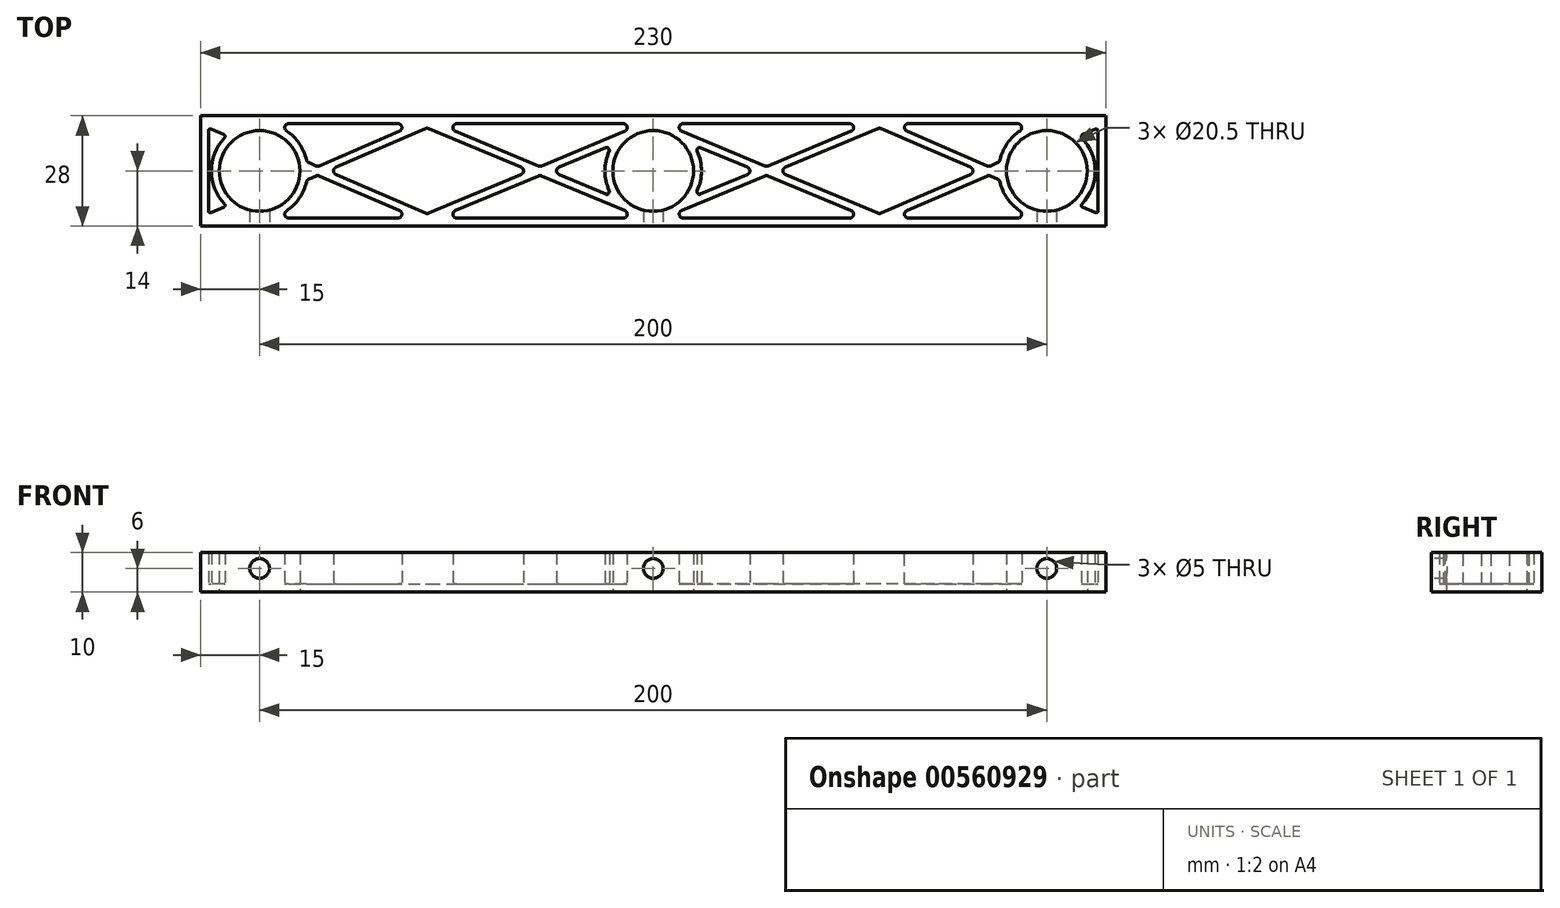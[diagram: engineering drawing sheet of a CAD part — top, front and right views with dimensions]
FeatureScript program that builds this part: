
annotation { "Feature Type Name" : "Feature", "Feature Type Description" : "" }
export const myFeature = defineFeature(function(context is Context, id is Id, definition is map)
    precondition{}
    {
        {
            var Q0;
            Q0=qCreatedBy(makeId("Top.planeOp"),FACE);
            var sketch = newSketch(context, id + "F0", { "sketchPlane" : qUnion([Q0])});
            skCircle(sketch, "E0", {"center": v(0, 0) * mm, "radius": 10.25 * mm});
            skCircle(sketch, "E1", {"center": v(-100, 0) * mm, "radius": 10.25 * mm});
            skLineSegment(sketch, "E2", {"start": v(0, 0) * mm, "end": v(0, 43.05) * mm, "construction": true});
            skCircle(sketch, "E3.MirrorC", {"center": v(100, 0) * mm, "radius": 10.25 * mm});
            skLineSegment(sketch, "E4", {"start": v(-100, 0) * mm, "end": v(0, 0) * mm, "construction": true});
            skLineSegment(sketch, "E5.bottom", {"start": v(115, -14) * mm, "end": v(-115, -14) * mm});
            skLineSegment(sketch, "E5.top", {"start": v(115, 14) * mm, "end": v(-115, 14) * mm});
            skLineSegment(sketch, "E5.left", {"start": v(115, -14) * mm, "end": v(115, 14) * mm});
            skLineSegment(sketch, "E5.right", {"start": v(-115, -14) * mm, "end": v(-115, 14) * mm});
            skSolve(sketch);
        }
        {
            var Q0;
            Q0=makeQuery(id+"F0.imprint","IMPRINT",FACE,{"disambiguationData":[TD([[makeQuery(id+"F0.imprint","IMPRINT",EDGE,{"derivedFrom":sQuery(id+"F0.wireOp",EDGE,"E0")}),-1.0]])]});
            extrude(context, id + "F1", {"entities" : qUnion([Q0]), "depth" : 2 * mm});
        }
        {
            var Q0;
            Q0=makeQuery(id+"F1.opExtrude","CAP_FACE",FACE,{"disambiguationData":[OSD([sQuery(id+"F0.wireOp",EDGE,"E0"),sQuery(id+"F0.wireOp",EDGE,"E1"),sQuery(id+"F0.wireOp",EDGE,"E3.MirrorC"),sQuery(id+"F0.wireOp",EDGE,"E5.bottom"),sQuery(id+"F0.wireOp",EDGE,"E5.top"),sQuery(id+"F0.wireOp",EDGE,"E5.left"),sQuery(id+"F0.wireOp",EDGE,"E5.right")])],"isStart":false});
            var sketch = newSketch(context, id + "F2", { "sketchPlane" : qUnion([Q0])});
            skLineSegment(sketch, "E6.0", {"start": v(115, 14) * mm, "end": v(-115, 14) * mm});
            skLineSegment(sketch, "E7.0", {"start": v(-115, -14) * mm, "end": v(-115, 14) * mm});
            skLineSegment(sketch, "E8.0", {"start": v(115, -14) * mm, "end": v(-115, -14) * mm});
            skLineSegment(sketch, "E9.0", {"start": v(115, -14) * mm, "end": v(115, 14) * mm});
            skLineSegment(sketch, "E10.bottom", {"start": v(-110.48, 12) * mm, "end": v(-102.46, 12) * mm, "construction": true});
            skLineSegment(sketch, "E10.top", {"start": v(-110.48, -12) * mm, "end": v(-102.46, -12) * mm, "construction": true});
            skLineSegment(sketch, "E10.left", {"start": v(-113, 10.91) * mm, "end": v(-113, -10.91) * mm});
            skLineSegment(sketch, "E10.right", {"start": v(113, 10.91) * mm, "end": v(113, -10.91) * mm});
            skPoint(sketch, "E10.middle", {"position": v(0, 0) * mm});
            skCircle(sketch, "E11.0", {"center": v(-100, 0) * mm, "radius": 10.25 * mm});
            skCircle(sketch, "E12.0", {"center": v(0, 0) * mm, "radius": 10.25 * mm});
            skCircle(sketch, "E13.0", {"center": v(100, 0) * mm, "radius": 10.25 * mm});
            skArc(sketch, "E14", {"start": v(-87.96, 2.26) * mm, "mid": v(-91.27, 8.59) * mm, "end": v(-97.54, 12) * mm});
            skArc(sketch, "E15", {"start": v(-11.1, 5.2) * mm, "mid": v(-12.25, 0) * mm, "end": v(-11.1, -5.2) * mm});
            skArc(sketch, "E16", {"start": v(106.6, 10.32) * mm, "mid": v(104.6, 11.35) * mm, "end": v(102.46, 12) * mm, "construction": true});
            skLineSegment(sketch, "E17", {"start": v(0, 29.32) * mm, "end": v(0, -26.43) * mm, "construction": true});
            skLineSegment(sketch, "E18", {"start": v(-57.5, -14) * mm, "end": v(-57.5, 14) * mm, "construction": true});
            skLineSegment(sketch, "E19.MirrorCS", {"start": v(57.5, -14) * mm, "end": v(57.5, 14) * mm, "construction": true});
            skLineSegment(sketch, "E20", {"start": v(-113, 12) * mm, "end": v(-57.5, -12) * mm, "construction": true});
            skLineSegment(sketch, "E21", {"start": v(-57.5, 12) * mm, "end": v(-113, -12) * mm, "construction": true});
            skLineSegment(sketch, "E22", {"start": v(-57.5, 12) * mm, "end": v(0, -12) * mm, "construction": true});
            skLineSegment(sketch, "E23", {"start": v(-57.5, -12) * mm, "end": v(0, 12) * mm, "construction": true});
            skLineSegment(sketch, "E24", {"start": v(-110.48, -12) * mm, "end": v(-106.6, -10.32) * mm, "construction": true});
            skLineSegment(sketch, "E25.MirrorCS", {"start": v(-111.27, -10.16) * mm, "end": v(-108.4, -8.92) * mm});
            skPoint(sketch, "E26.orphan", {"position": v(-58.3, 12.75) * mm});
            skLineSegment(sketch, "E27", {"start": v(-111.27, -10.16) * mm, "end": v(-113, -10.91) * mm});
            skLineSegment(sketch, "E28", {"start": v(-110.48, 12) * mm, "end": v(-106.6, 10.32) * mm, "construction": true});
            skLineSegment(sketch, "E29.MirrorCS", {"start": v(-111.27, 10.16) * mm, "end": v(-108.4, 8.92) * mm});
            skLineSegment(sketch, "E30", {"start": v(-111.27, 10.16) * mm, "end": v(-113, 10.91) * mm});
            skPoint(sketch, "E31.orphan", {"position": v(-58.3, -12.75) * mm});
            skLineSegment(sketch, "E32.trimOffspring", {"start": v(-85.25, 1.09) * mm, "end": v(-60.02, 12) * mm});
            skLineSegment(sketch, "E33.trimOffspring", {"start": v(-82.73, 0) * mm, "end": v(-57.5, -10.91) * mm});
            skLineSegment(sketch, "E34.trimOffspring", {"start": v(-82.73, 0) * mm, "end": v(-57.5, 10.91) * mm});
            skLineSegment(sketch, "E35.trimOffspring", {"start": v(-85.25, -1.09) * mm, "end": v(-60.02, -12) * mm});
            skLineSegment(sketch, "E36.trimOffspring", {"start": v(-87.96, 2.26) * mm, "end": v(-85.25, 1.09) * mm});
            skLineSegment(sketch, "E37.trimOffspring", {"start": v(-87.96, -2.26) * mm, "end": v(-85.25, -1.09) * mm});
            skArc(sketch, "E38.trimOffspring", {"start": v(-108.4, 8.92) * mm, "mid": v(-112.25, 0) * mm, "end": v(-108.4, -8.92) * mm});
            skArc(sketch, "E39.trimOffspring", {"start": v(-106.6, -10.32) * mm, "mid": v(-104.6, -11.35) * mm, "end": v(-102.46, -12) * mm, "construction": true});
            skLineSegment(sketch, "E40", {"start": v(-57.5, 10.91) * mm, "end": v(-31.36, 0) * mm});
            skLineSegment(sketch, "E41.MirrorCS", {"start": v(-54.89, 12) * mm, "end": v(-28.75, 1.09) * mm});
            skPoint(sketch, "E42.orphan", {"position": v(-56.73, 12.77) * mm});
            skLineSegment(sketch, "E43.trimOffspring", {"start": v(-54.89, 12) * mm, "end": v(-2.61, 12) * mm});
            skLineSegment(sketch, "E44", {"start": v(-57.5, -10.91) * mm, "end": v(-31.36, 0) * mm});
            skLineSegment(sketch, "E45.MirrorCS", {"start": v(-54.89, -12) * mm, "end": v(-28.75, -1.09) * mm});
            skPoint(sketch, "E46.orphan", {"position": v(-56.73, -12.77) * mm});
            skLineSegment(sketch, "E47.trimOffspring", {"start": v(-54.89, -12) * mm, "end": v(-2.61, -12) * mm});
            skLineSegment(sketch, "E48", {"start": v(-11.48, 6.12) * mm, "end": v(-11.1, 5.2) * mm});
            skPoint(sketch, "E49.orphan", {"position": v(-1.84, 10.14) * mm});
            skLineSegment(sketch, "E50", {"start": v(-11.48, -6.12) * mm, "end": v(-11.1, -5.2) * mm});
            skPoint(sketch, "E51.orphan", {"position": v(-1.84, -10.14) * mm});
            skLineSegment(sketch, "E52.trimOffspring", {"start": v(-28.75, 1.09) * mm, "end": v(-2.61, 12) * mm});
            skLineSegment(sketch, "E53.trimOffspring", {"start": v(-26.14, 0) * mm, "end": v(-11.48, -6.12) * mm});
            skLineSegment(sketch, "E54.trimOffspring", {"start": v(-26.14, 0) * mm, "end": v(-11.48, 6.12) * mm});
            skLineSegment(sketch, "E55.trimOffspring", {"start": v(-28.75, -1.09) * mm, "end": v(-2.61, -12) * mm});
            skLineSegment(sketch, "E56.trimOffspring", {"start": v(2.61, 12) * mm, "end": v(54.89, 12) * mm});
            skLineSegment(sketch, "E57.MirrorCS", {"start": v(110.48, -12) * mm, "end": v(102.46, -12) * mm});
            skLineSegment(sketch, "E58.MirrorCS", {"start": v(110.48, -12) * mm, "end": v(106.6, -10.32) * mm, "construction": true});
            skLineSegment(sketch, "E59.MirrorCS", {"start": v(111.27, -10.16) * mm, "end": v(113, -10.91) * mm});
            skLineSegment(sketch, "E60.MirrorCS", {"start": v(111.27, -10.16) * mm, "end": v(108.4, -8.92) * mm});
            skLineSegment(sketch, "E61.MirrorCS", {"start": v(111.27, 10.16) * mm, "end": v(113, 10.91) * mm});
            skLineSegment(sketch, "E62.MirrorCS", {"start": v(111.27, 10.16) * mm, "end": v(108.4, 8.92) * mm});
            skLineSegment(sketch, "E63.MirrorCS", {"start": v(110.48, 12) * mm, "end": v(102.46, 12) * mm});
            skLineSegment(sketch, "E64.MirrorCS", {"start": v(110.48, 12) * mm, "end": v(106.6, 10.32) * mm, "construction": true});
            skLineSegment(sketch, "E65.MirrorCS", {"start": v(87.96, 2.26) * mm, "end": v(85.25, 1.09) * mm});
            skLineSegment(sketch, "E66.MirrorCS", {"start": v(87.96, -2.26) * mm, "end": v(85.25, -1.09) * mm});
            skLineSegment(sketch, "E67.MirrorCS", {"start": v(85.25, -1.09) * mm, "end": v(60.02, -12) * mm});
            skLineSegment(sketch, "E68.MirrorCS", {"start": v(85.25, 1.09) * mm, "end": v(60.02, 12) * mm});
            skLineSegment(sketch, "E69.MirrorCS", {"start": v(82.73, 0) * mm, "end": v(57.5, -10.91) * mm});
            skLineSegment(sketch, "E70.MirrorCS", {"start": v(82.73, 0) * mm, "end": v(57.5, 10.91) * mm});
            skLineSegment(sketch, "E71.MirrorCS", {"start": v(57.5, -10.91) * mm, "end": v(31.36, 0) * mm});
            skLineSegment(sketch, "E72.MirrorCS", {"start": v(54.89, 12) * mm, "end": v(2.61, 12) * mm});
            skLineSegment(sketch, "E73.MirrorCS", {"start": v(54.89, 12) * mm, "end": v(28.75, 1.09) * mm});
            skLineSegment(sketch, "E74.MirrorCS", {"start": v(57.5, 10.91) * mm, "end": v(31.36, 0) * mm});
            skLineSegment(sketch, "E75.MirrorCS", {"start": v(54.89, -12) * mm, "end": v(28.75, -1.09) * mm});
            skLineSegment(sketch, "E76.MirrorCS", {"start": v(54.89, -12) * mm, "end": v(2.61, -12) * mm});
            skLineSegment(sketch, "E77.MirrorCS", {"start": v(28.75, -1.09) * mm, "end": v(2.61, -12) * mm});
            skLineSegment(sketch, "E78.MirrorCS", {"start": v(11.48, -6.12) * mm, "end": v(11.1, -5.2) * mm});
            skLineSegment(sketch, "E79.MirrorCS", {"start": v(26.14, 0) * mm, "end": v(11.48, -6.12) * mm});
            skLineSegment(sketch, "E80.MirrorCS", {"start": v(26.14, 0) * mm, "end": v(11.48, 6.12) * mm});
            skLineSegment(sketch, "E81.MirrorCS", {"start": v(11.48, 6.12) * mm, "end": v(11.1, 5.2) * mm});
            skLineSegment(sketch, "E82.MirrorCS", {"start": v(28.75, 1.09) * mm, "end": v(2.61, 12) * mm});
            skArc(sketch, "E83.trimOffspring", {"start": v(11.1, -5.2) * mm, "mid": v(12.25, 0) * mm, "end": v(11.1, 5.2) * mm});
            skLineSegment(sketch, "E84.trimOffspring", {"start": v(60.02, 12) * mm, "end": v(97.54, 12) * mm});
            skLineSegment(sketch, "E85.trimOffspring", {"start": v(60.02, -12) * mm, "end": v(97.54, -12) * mm});
            skPoint(sketch, "E86.orphan", {"position": v(113, -12) * mm});
            skPoint(sketch, "E87.orphan", {"position": v(113, 12) * mm});
            skArc(sketch, "E88.trimOffspring", {"start": v(87.96, -2.26) * mm, "mid": v(91.27, -8.59) * mm, "end": v(97.54, -12) * mm});
            skArc(sketch, "E89.trimOffspring", {"start": v(108.4, -8.92) * mm, "mid": v(112.25, 0) * mm, "end": v(108.4, 8.92) * mm});
            skArc(sketch, "E90.trimOffspring", {"start": v(102.46, -12) * mm, "mid": v(104.6, -11.35) * mm, "end": v(106.6, -10.32) * mm, "construction": true});
            skLineSegment(sketch, "E91.trimOffspring", {"start": v(97.54, -12) * mm, "end": v(60.02, -12) * mm});
            skLineSegment(sketch, "E92.trimOffspring", {"start": v(102.46, -12) * mm, "end": v(110.48, -12) * mm, "construction": true});
            skLineSegment(sketch, "E93.trimOffspring", {"start": v(97.54, 12) * mm, "end": v(60.02, 12) * mm});
            skLineSegment(sketch, "E94.trimOffspring", {"start": v(102.46, 12) * mm, "end": v(110.48, 12) * mm, "construction": true});
            skArc(sketch, "E95.trimOffspring", {"start": v(97.54, 12) * mm, "mid": v(91.27, 8.59) * mm, "end": v(87.96, 2.26) * mm});
            skArc(sketch, "E96.trimOffspring", {"start": v(-102.46, 12) * mm, "mid": v(-104.6, 11.35) * mm, "end": v(-106.6, 10.32) * mm, "construction": true});
            skLineSegment(sketch, "E97.trimOffspring", {"start": v(-97.54, 12) * mm, "end": v(-60.02, 12) * mm});
            skArc(sketch, "E98.trimOffspring", {"start": v(-97.54, -12) * mm, "mid": v(-91.27, -8.59) * mm, "end": v(-87.96, -2.26) * mm});
            skLineSegment(sketch, "E99.trimOffspring", {"start": v(-97.54, -12) * mm, "end": v(-60.02, -12) * mm});
            skSolve(sketch);
        }
        {
            var Q0;
            Q0=qSketchRegion(id+"F2",true);
            extrude(context, id + "F3", {"entities" : qUnion([Q0]), "operationType" : NewBodyOperationType.ADD, "depth" : 8 * mm});
        }
        {
            var Q0;
            Q0=makeQuery(id+"F3.boolean.opBoolean","MERGE",FACE,{"derivedFrom":[makeQuery(id+"F1.opExtrude","SWEPT_FACE",FACE,{"disambiguationData":[OSD([sQuery(id+"F0.wireOp",EDGE,"E5.bottom")])]}),makeQuery(id+"F3.opExtrude","SWEPT_FACE",FACE,{"disambiguationData":[OSD([sQuery(id+"F2.wireOp",EDGE,"E8.0")])]})]});
            var sketch = newSketch(context, id + "F4", { "sketchPlane" : qUnion([Q0])});
            skLineSegment(sketch, "E100.0", {"start": v(-110.25, 0) * mm, "end": v(-89.75, 0) * mm, "construction": true});
            skLineSegment(sketch, "E101.0", {"start": v(-10.25, 0) * mm, "end": v(10.25, 0) * mm, "construction": true});
            skLineSegment(sketch, "E102.0", {"start": v(110.25, 0) * mm, "end": v(89.75, 0) * mm, "construction": true});
            skLineSegment(sketch, "E103", {"start": v(-100, 0) * mm, "end": v(-100, 10) * mm, "construction": true});
            skLineSegment(sketch, "E104", {"start": v(0, 0) * mm, "end": v(0, 10) * mm, "construction": true});
            skLineSegment(sketch, "E105", {"start": v(100, 0) * mm, "end": v(100, 10) * mm, "construction": true});
            skCircle(sketch, "E106", {"center": v(-100, 6) * mm, "radius": 2.5 * mm});
            skLineSegment(sketch, "E107", {"start": v(-100, 6) * mm, "end": v(0, 6) * mm, "construction": true});
            skLineSegment(sketch, "E108", {"start": v(0, 6) * mm, "end": v(100, 6) * mm, "construction": true});
            skCircle(sketch, "E109", {"center": v(0, 6) * mm, "radius": 2.5 * mm});
            skCircle(sketch, "E110", {"center": v(100, 6) * mm, "radius": 2.5 * mm});
            skSolve(sketch);
        }
        {
            var Q0;
            Q0=qSketchRegion(id+"F4",true);
            extrude(context, id + "F5", {"entities" : qUnion([Q0]), "operationType" : NewBodyOperationType.REMOVE, "oppositeDirection" : true, "depth" : 10 * mm});
        }
        {
            var Q0;
            Q0=makeQuery(id+"F3.opExtrude","SWEPT_EDGE",EDGE,{"disambiguationData":[OSD([sQuery(id+"F2.wireOp",EDGE,"E14"),sQuery(id+"F2.wireOp",EDGE,"E97.trimOffspring")])]});
            var Q1;
            {var subQ0=sQuery(id+"F2.wireOp",EDGE,"E99.trimOffspring");var subQ1=sQuery(id+"F2.wireOp",EDGE,"E98.trimOffspring");Q1=makeQuery(id+"F5.boolean.opBoolean","SPLIT",EDGE,{"disambiguationData":[TD([makeQuery(id+"F3.opExtrude","CAP_FACE",FACE,{"disambiguationData":[OSD([sQuery(id+"F2.wireOp",EDGE,"E6.0"),sQuery(id+"F2.wireOp",EDGE,"E7.0"),sQuery(id+"F2.wireOp",EDGE,"E8.0"),sQuery(id+"F2.wireOp",EDGE,"E9.0"),sQuery(id+"F2.wireOp",EDGE,"E10.left"),sQuery(id+"F2.wireOp",EDGE,"E10.right"),sQuery(id+"F2.wireOp",EDGE,"E11.0"),sQuery(id+"F2.wireOp",EDGE,"E12.0"),sQuery(id+"F2.wireOp",EDGE,"E13.0"),sQuery(id+"F2.wireOp",EDGE,"E14"),sQuery(id+"F2.wireOp",EDGE,"E15"),sQuery(id+"F2.wireOp",EDGE,"E25.MirrorCS"),sQuery(id+"F2.wireOp",EDGE,"E27"),sQuery(id+"F2.wireOp",EDGE,"E29.MirrorCS"),sQuery(id+"F2.wireOp",EDGE,"E30"),sQuery(id+"F2.wireOp",EDGE,"E32.trimOffspring"),sQuery(id+"F2.wireOp",EDGE,"E33.trimOffspring"),sQuery(id+"F2.wireOp",EDGE,"E34.trimOffspring"),sQuery(id+"F2.wireOp",EDGE,"E35.trimOffspring"),sQuery(id+"F2.wireOp",EDGE,"E36.trimOffspring"),sQuery(id+"F2.wireOp",EDGE,"E37.trimOffspring"),sQuery(id+"F2.wireOp",EDGE,"E38.trimOffspring"),sQuery(id+"F2.wireOp",EDGE,"E40"),sQuery(id+"F2.wireOp",EDGE,"E41.MirrorCS"),sQuery(id+"F2.wireOp",EDGE,"E43.trimOffspring"),sQuery(id+"F2.wireOp",EDGE,"E44"),sQuery(id+"F2.wireOp",EDGE,"E45.MirrorCS"),sQuery(id+"F2.wireOp",EDGE,"E47.trimOffspring"),sQuery(id+"F2.wireOp",EDGE,"E48"),sQuery(id+"F2.wireOp",EDGE,"E50"),sQuery(id+"F2.wireOp",EDGE,"E52.trimOffspring"),sQuery(id+"F2.wireOp",EDGE,"E53.trimOffspring"),sQuery(id+"F2.wireOp",EDGE,"E54.trimOffspring"),sQuery(id+"F2.wireOp",EDGE,"E55.trimOffspring"),sQuery(id+"F2.wireOp",EDGE,"E59.MirrorCS"),sQuery(id+"F2.wireOp",EDGE,"E60.MirrorCS"),sQuery(id+"F2.wireOp",EDGE,"E61.MirrorCS"),sQuery(id+"F2.wireOp",EDGE,"E62.MirrorCS"),sQuery(id+"F2.wireOp",EDGE,"E65.MirrorCS"),sQuery(id+"F2.wireOp",EDGE,"E66.MirrorCS"),sQuery(id+"F2.wireOp",EDGE,"E67.MirrorCS"),sQuery(id+"F2.wireOp",EDGE,"E68.MirrorCS"),sQuery(id+"F2.wireOp",EDGE,"E69.MirrorCS"),sQuery(id+"F2.wireOp",EDGE,"E70.MirrorCS"),sQuery(id+"F2.wireOp",EDGE,"E71.MirrorCS"),sQuery(id+"F2.wireOp",EDGE,"E72.MirrorCS"),sQuery(id+"F2.wireOp",EDGE,"E73.MirrorCS"),sQuery(id+"F2.wireOp",EDGE,"E74.MirrorCS"),sQuery(id+"F2.wireOp",EDGE,"E75.MirrorCS"),sQuery(id+"F2.wireOp",EDGE,"E76.MirrorCS"),sQuery(id+"F2.wireOp",EDGE,"E77.MirrorCS"),sQuery(id+"F2.wireOp",EDGE,"E78.MirrorCS"),sQuery(id+"F2.wireOp",EDGE,"E79.MirrorCS"),sQuery(id+"F2.wireOp",EDGE,"E80.MirrorCS"),sQuery(id+"F2.wireOp",EDGE,"E81.MirrorCS"),sQuery(id+"F2.wireOp",EDGE,"E82.MirrorCS"),sQuery(id+"F2.wireOp",EDGE,"E83.trimOffspring"),sQuery(id+"F2.wireOp",EDGE,"E88.trimOffspring"),sQuery(id+"F2.wireOp",EDGE,"E89.trimOffspring"),sQuery(id+"F2.wireOp",EDGE,"E91.trimOffspring"),sQuery(id+"F2.wireOp",EDGE,"E93.trimOffspring"),sQuery(id+"F2.wireOp",EDGE,"E95.trimOffspring"),sQuery(id+"F2.wireOp",EDGE,"E97.trimOffspring"),subQ1,subQ0])],"isStart":false})])],"derivedFrom":makeQuery(id+"F3.opExtrude","SWEPT_EDGE",EDGE,{"disambiguationData":[OSD([subQ1,subQ0])]})});}
            var Q2;
            Q2=makeQuery(id+"F3.opExtrude","SWEPT_EDGE",EDGE,{"disambiguationData":[OSD([sQuery(id+"F2.wireOp",EDGE,"E32.trimOffspring"),sQuery(id+"F2.wireOp",EDGE,"E97.trimOffspring")])]});
            var Q3;
            Q3=makeQuery(id+"F3.opExtrude","SWEPT_EDGE",EDGE,{"disambiguationData":[OSD([sQuery(id+"F2.wireOp",EDGE,"E41.MirrorCS"),sQuery(id+"F2.wireOp",EDGE,"E43.trimOffspring")])]});
            var Q4;
            Q4=makeQuery(id+"F3.opExtrude","SWEPT_EDGE",EDGE,{"disambiguationData":[OSD([sQuery(id+"F2.wireOp",EDGE,"E45.MirrorCS"),sQuery(id+"F2.wireOp",EDGE,"E47.trimOffspring")])]});
            var Q5;
            Q5=makeQuery(id+"F3.opExtrude","SWEPT_EDGE",EDGE,{"disambiguationData":[OSD([sQuery(id+"F2.wireOp",EDGE,"E35.trimOffspring"),sQuery(id+"F2.wireOp",EDGE,"E99.trimOffspring")])]});
            var Q6;
            Q6=makeQuery(id+"F3.opExtrude","SWEPT_EDGE",EDGE,{"disambiguationData":[OSD([sQuery(id+"F2.wireOp",EDGE,"E72.MirrorCS"),sQuery(id+"F2.wireOp",EDGE,"E73.MirrorCS")])]});
            var Q7;
            Q7=makeQuery(id+"F3.opExtrude","SWEPT_EDGE",EDGE,{"disambiguationData":[OSD([sQuery(id+"F2.wireOp",EDGE,"E75.MirrorCS"),sQuery(id+"F2.wireOp",EDGE,"E76.MirrorCS")])]});
            var Q8;
            Q8=makeQuery(id+"F3.opExtrude","SWEPT_EDGE",EDGE,{"disambiguationData":[OSD([sQuery(id+"F2.wireOp",EDGE,"E68.MirrorCS"),sQuery(id+"F2.wireOp",EDGE,"E93.trimOffspring")])]});
            var Q9;
            Q9=makeQuery(id+"F3.opExtrude","SWEPT_EDGE",EDGE,{"disambiguationData":[OSD([sQuery(id+"F2.wireOp",EDGE,"E67.MirrorCS"),sQuery(id+"F2.wireOp",EDGE,"E91.trimOffspring")])]});
            var Q10;
            Q10=makeQuery(id+"F3.opExtrude","SWEPT_EDGE",EDGE,{"disambiguationData":[OSD([sQuery(id+"F2.wireOp",EDGE,"E93.trimOffspring"),sQuery(id+"F2.wireOp",EDGE,"E95.trimOffspring")])]});
            var Q11;
            {var subQ0=sQuery(id+"F2.wireOp",EDGE,"E88.trimOffspring");var subQ1=sQuery(id+"F2.wireOp",EDGE,"E91.trimOffspring");Q11=makeQuery(id+"F5.boolean.opBoolean","SPLIT",EDGE,{"disambiguationData":[TD([makeQuery(id+"F1.opExtrude","CAP_FACE",FACE,{"disambiguationData":[OSD([sQuery(id+"F0.wireOp",EDGE,"E0"),sQuery(id+"F0.wireOp",EDGE,"E1"),sQuery(id+"F0.wireOp",EDGE,"E3.MirrorC"),sQuery(id+"F0.wireOp",EDGE,"E5.bottom"),sQuery(id+"F0.wireOp",EDGE,"E5.top"),sQuery(id+"F0.wireOp",EDGE,"E5.left"),sQuery(id+"F0.wireOp",EDGE,"E5.right")])],"isStart":false})])],"derivedFrom":makeQuery(id+"F3.opExtrude","SWEPT_EDGE",EDGE,{"disambiguationData":[OSD([subQ0,subQ1])]})});}
            var Q12;
            Q12=makeQuery(id+"F3.opExtrude","SWEPT_EDGE",EDGE,{"disambiguationData":[OSD([sQuery(id+"F2.wireOp",EDGE,"E34.trimOffspring"),sQuery(id+"F2.wireOp",EDGE,"E40")])]});
            var Q13;
            Q13=makeQuery(id+"F3.opExtrude","SWEPT_EDGE",EDGE,{"disambiguationData":[OSD([sQuery(id+"F2.wireOp",EDGE,"E33.trimOffspring"),sQuery(id+"F2.wireOp",EDGE,"E44")])]});
            var Q14;
            Q14=makeQuery(id+"F3.opExtrude","SWEPT_EDGE",EDGE,{"disambiguationData":[OSD([sQuery(id+"F2.wireOp",EDGE,"E40"),sQuery(id+"F2.wireOp",EDGE,"E44")])]});
            var Q15;
            Q15=makeQuery(id+"F3.opExtrude","SWEPT_EDGE",EDGE,{"disambiguationData":[OSD([sQuery(id+"F2.wireOp",EDGE,"E53.trimOffspring"),sQuery(id+"F2.wireOp",EDGE,"E54.trimOffspring")])]});
            var Q16;
            Q16=makeQuery(id+"F3.opExtrude","SWEPT_EDGE",EDGE,{"disambiguationData":[OSD([sQuery(id+"F2.wireOp",EDGE,"E41.MirrorCS"),sQuery(id+"F2.wireOp",EDGE,"E52.trimOffspring")])]});
            var Q17;
            Q17=makeQuery(id+"F3.opExtrude","SWEPT_EDGE",EDGE,{"disambiguationData":[OSD([sQuery(id+"F2.wireOp",EDGE,"E45.MirrorCS"),sQuery(id+"F2.wireOp",EDGE,"E55.trimOffspring")])]});
            var Q18;
            Q18=makeQuery(id+"F3.opExtrude","SWEPT_EDGE",EDGE,{"disambiguationData":[OSD([sQuery(id+"F2.wireOp",EDGE,"E33.trimOffspring"),sQuery(id+"F2.wireOp",EDGE,"E34.trimOffspring")])]});
            var Q19;
            Q19=makeQuery(id+"F3.opExtrude","SWEPT_EDGE",EDGE,{"disambiguationData":[OSD([sQuery(id+"F2.wireOp",EDGE,"E71.MirrorCS"),sQuery(id+"F2.wireOp",EDGE,"E74.MirrorCS")])]});
            var Q20;
            Q20=makeQuery(id+"F3.opExtrude","SWEPT_EDGE",EDGE,{"disambiguationData":[OSD([sQuery(id+"F2.wireOp",EDGE,"E79.MirrorCS"),sQuery(id+"F2.wireOp",EDGE,"E80.MirrorCS")])]});
            var Q21;
            Q21=makeQuery(id+"F3.opExtrude","SWEPT_EDGE",EDGE,{"disambiguationData":[OSD([sQuery(id+"F2.wireOp",EDGE,"E69.MirrorCS"),sQuery(id+"F2.wireOp",EDGE,"E70.MirrorCS")])]});
            var Q22;
            Q22=makeQuery(id+"F3.opExtrude","SWEPT_EDGE",EDGE,{"disambiguationData":[OSD([sQuery(id+"F2.wireOp",EDGE,"E72.MirrorCS"),sQuery(id+"F2.wireOp",EDGE,"E82.MirrorCS")])]});
            var Q23;
            Q23=makeQuery(id+"F3.opExtrude","SWEPT_EDGE",EDGE,{"disambiguationData":[OSD([sQuery(id+"F2.wireOp",EDGE,"E43.trimOffspring"),sQuery(id+"F2.wireOp",EDGE,"E52.trimOffspring")])]});
            var Q24;
            Q24=makeQuery(id+"F3.opExtrude","SWEPT_EDGE",EDGE,{"disambiguationData":[OSD([sQuery(id+"F2.wireOp",EDGE,"E47.trimOffspring"),sQuery(id+"F2.wireOp",EDGE,"E55.trimOffspring")])]});
            var Q25;
            Q25=makeQuery(id+"F3.opExtrude","SWEPT_EDGE",EDGE,{"disambiguationData":[OSD([sQuery(id+"F2.wireOp",EDGE,"E76.MirrorCS"),sQuery(id+"F2.wireOp",EDGE,"E77.MirrorCS")])]});
            var Q26;
            Q26=makeQuery(id+"F3.opExtrude","SWEPT_EDGE",EDGE,{"disambiguationData":[OSD([sQuery(id+"F2.wireOp",EDGE,"E14"),sQuery(id+"F2.wireOp",EDGE,"E36.trimOffspring")])]});
            var Q27;
            Q27=makeQuery(id+"F3.opExtrude","SWEPT_EDGE",EDGE,{"disambiguationData":[OSD([sQuery(id+"F2.wireOp",EDGE,"E32.trimOffspring"),sQuery(id+"F2.wireOp",EDGE,"E36.trimOffspring")])]});
            var Q28;
            Q28=makeQuery(id+"F3.opExtrude","SWEPT_EDGE",EDGE,{"disambiguationData":[OSD([sQuery(id+"F2.wireOp",EDGE,"E35.trimOffspring"),sQuery(id+"F2.wireOp",EDGE,"E37.trimOffspring")])]});
            var Q29;
            Q29=makeQuery(id+"F3.opExtrude","SWEPT_EDGE",EDGE,{"disambiguationData":[OSD([sQuery(id+"F2.wireOp",EDGE,"E37.trimOffspring"),sQuery(id+"F2.wireOp",EDGE,"E98.trimOffspring")])]});
            var Q30;
            Q30=makeQuery(id+"F3.opExtrude","SWEPT_EDGE",EDGE,{"disambiguationData":[OSD([sQuery(id+"F2.wireOp",EDGE,"E66.MirrorCS"),sQuery(id+"F2.wireOp",EDGE,"E67.MirrorCS")])]});
            var Q31;
            Q31=makeQuery(id+"F3.opExtrude","SWEPT_EDGE",EDGE,{"disambiguationData":[OSD([sQuery(id+"F2.wireOp",EDGE,"E66.MirrorCS"),sQuery(id+"F2.wireOp",EDGE,"E88.trimOffspring")])]});
            var Q32;
            Q32=makeQuery(id+"F3.opExtrude","SWEPT_EDGE",EDGE,{"disambiguationData":[OSD([sQuery(id+"F2.wireOp",EDGE,"E65.MirrorCS"),sQuery(id+"F2.wireOp",EDGE,"E68.MirrorCS")])]});
            var Q33;
            Q33=makeQuery(id+"F3.opExtrude","SWEPT_EDGE",EDGE,{"disambiguationData":[OSD([sQuery(id+"F2.wireOp",EDGE,"E65.MirrorCS"),sQuery(id+"F2.wireOp",EDGE,"E95.trimOffspring")])]});
            var Q34;
            Q34=makeQuery(id+"F3.opExtrude","SWEPT_EDGE",EDGE,{"disambiguationData":[OSD([sQuery(id+"F2.wireOp",EDGE,"E69.MirrorCS"),sQuery(id+"F2.wireOp",EDGE,"E71.MirrorCS")])]});
            var Q35;
            Q35=makeQuery(id+"F3.opExtrude","SWEPT_EDGE",EDGE,{"disambiguationData":[OSD([sQuery(id+"F2.wireOp",EDGE,"E70.MirrorCS"),sQuery(id+"F2.wireOp",EDGE,"E74.MirrorCS")])]});
            var Q36;
            Q36=makeQuery(id+"F3.opExtrude","SWEPT_EDGE",EDGE,{"disambiguationData":[OSD([sQuery(id+"F2.wireOp",EDGE,"E75.MirrorCS"),sQuery(id+"F2.wireOp",EDGE,"E77.MirrorCS")])]});
            var Q37;
            Q37=makeQuery(id+"F3.opExtrude","SWEPT_EDGE",EDGE,{"disambiguationData":[OSD([sQuery(id+"F2.wireOp",EDGE,"E73.MirrorCS"),sQuery(id+"F2.wireOp",EDGE,"E82.MirrorCS")])]});
            fillet(context, id + "F6", {"entities" : qUnion([Q0, Q1, Q2, Q3, Q4, Q5, Q6, Q7, Q8, Q9, Q10, Q11, Q12, Q13, Q14, Q15, Q16, Q17, Q18, Q19, Q20, Q21, Q22, Q23, Q24, Q25, Q26, Q27, Q28, Q29, Q30, Q31, Q32, Q33, Q34, Q35, Q36, Q37]), "radius" : 1 * mm, "tangentPropagation" : true, "allowEdgeOverflow" : false});
        }
        {
            var Q0;
            Q0=makeQuery(id+"F3.opExtrude","SWEPT_EDGE",EDGE,{"disambiguationData":[OSD([sQuery(id+"F2.wireOp",EDGE,"E10.left"),sQuery(id+"F2.wireOp",EDGE,"E30")])]});
            var Q1;
            Q1=makeQuery(id+"F3.opExtrude","SWEPT_EDGE",EDGE,{"disambiguationData":[OSD([sQuery(id+"F2.wireOp",EDGE,"E29.MirrorCS"),sQuery(id+"F2.wireOp",EDGE,"E38.trimOffspring")])]});
            var Q2;
            Q2=makeQuery(id+"F3.opExtrude","SWEPT_EDGE",EDGE,{"disambiguationData":[OSD([sQuery(id+"F2.wireOp",EDGE,"E25.MirrorCS"),sQuery(id+"F2.wireOp",EDGE,"E38.trimOffspring")])]});
            var Q3;
            Q3=makeQuery(id+"F3.opExtrude","SWEPT_EDGE",EDGE,{"disambiguationData":[OSD([sQuery(id+"F2.wireOp",EDGE,"E10.left"),sQuery(id+"F2.wireOp",EDGE,"E27")])]});
            var Q4;
            Q4=makeQuery(id+"F3.opExtrude","SWEPT_EDGE",EDGE,{"disambiguationData":[OSD([sQuery(id+"F2.wireOp",EDGE,"E10.right"),sQuery(id+"F2.wireOp",EDGE,"E61.MirrorCS")])]});
            var Q5;
            Q5=makeQuery(id+"F3.opExtrude","SWEPT_EDGE",EDGE,{"disambiguationData":[OSD([sQuery(id+"F2.wireOp",EDGE,"E62.MirrorCS"),sQuery(id+"F2.wireOp",EDGE,"E89.trimOffspring")])]});
            var Q6;
            Q6=makeQuery(id+"F3.opExtrude","SWEPT_EDGE",EDGE,{"disambiguationData":[OSD([sQuery(id+"F2.wireOp",EDGE,"E60.MirrorCS"),sQuery(id+"F2.wireOp",EDGE,"E89.trimOffspring")])]});
            var Q7;
            Q7=makeQuery(id+"F3.opExtrude","SWEPT_EDGE",EDGE,{"disambiguationData":[OSD([sQuery(id+"F2.wireOp",EDGE,"E10.right"),sQuery(id+"F2.wireOp",EDGE,"E59.MirrorCS")])]});
            var Q8;
            Q8=makeQuery(id+"F3.opExtrude","SWEPT_EDGE",EDGE,{"disambiguationData":[OSD([sQuery(id+"F2.wireOp",EDGE,"E48"),sQuery(id+"F2.wireOp",EDGE,"E54.trimOffspring")])]});
            var Q9;
            Q9=makeQuery(id+"F3.opExtrude","SWEPT_EDGE",EDGE,{"disambiguationData":[OSD([sQuery(id+"F2.wireOp",EDGE,"E15"),sQuery(id+"F2.wireOp",EDGE,"E48")])]});
            var Q10;
            Q10=makeQuery(id+"F3.opExtrude","SWEPT_EDGE",EDGE,{"disambiguationData":[OSD([sQuery(id+"F2.wireOp",EDGE,"E50"),sQuery(id+"F2.wireOp",EDGE,"E53.trimOffspring")])]});
            var Q11;
            Q11=makeQuery(id+"F3.opExtrude","SWEPT_EDGE",EDGE,{"disambiguationData":[OSD([sQuery(id+"F2.wireOp",EDGE,"E15"),sQuery(id+"F2.wireOp",EDGE,"E50")])]});
            var Q12;
            Q12=makeQuery(id+"F3.opExtrude","SWEPT_EDGE",EDGE,{"disambiguationData":[OSD([sQuery(id+"F2.wireOp",EDGE,"E78.MirrorCS"),sQuery(id+"F2.wireOp",EDGE,"E83.trimOffspring")])]});
            var Q13;
            Q13=makeQuery(id+"F3.opExtrude","SWEPT_EDGE",EDGE,{"disambiguationData":[OSD([sQuery(id+"F2.wireOp",EDGE,"E81.MirrorCS"),sQuery(id+"F2.wireOp",EDGE,"E83.trimOffspring")])]});
            var Q14;
            Q14=makeQuery(id+"F3.opExtrude","SWEPT_EDGE",EDGE,{"disambiguationData":[OSD([sQuery(id+"F2.wireOp",EDGE,"E80.MirrorCS"),sQuery(id+"F2.wireOp",EDGE,"E81.MirrorCS")])]});
            var Q15;
            Q15=makeQuery(id+"F3.opExtrude","SWEPT_EDGE",EDGE,{"disambiguationData":[OSD([sQuery(id+"F2.wireOp",EDGE,"E78.MirrorCS"),sQuery(id+"F2.wireOp",EDGE,"E79.MirrorCS")])]});
            fillet(context, id + "F7", {"entities" : qUnion([Q0, Q1, Q2, Q3, Q4, Q5, Q6, Q7, Q8, Q9, Q10, Q11, Q12, Q13, Q14, Q15]), "radius" : .5 * mm, "tangentPropagation" : true, "allowEdgeOverflow" : false});
        }
    });
